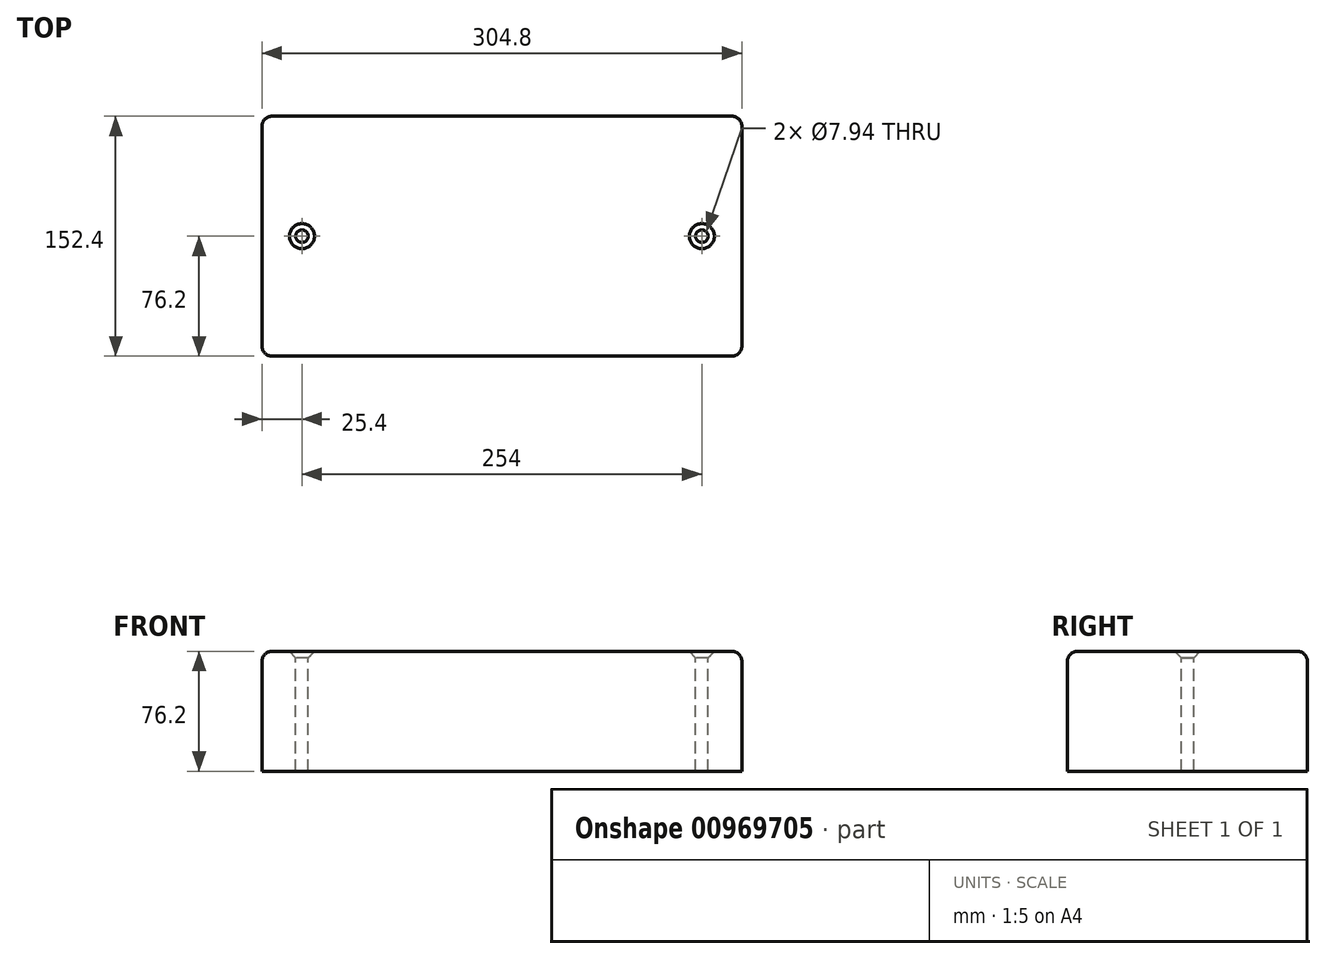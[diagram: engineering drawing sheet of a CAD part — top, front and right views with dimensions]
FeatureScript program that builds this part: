
annotation { "Feature Type Name" : "Feature", "Feature Type Description" : "" }
export const myFeature = defineFeature(function(context is Context, id is Id, definition is map)
    precondition{}
    {
        {
            var Q0;
            Q0=qCreatedBy(makeId("Top.planeOp"),FACE);
            var sketch = newSketch(context, id + "F0", { "sketchPlane" : qUnion([Q0])});
            skLineSegment(sketch, "E0.bottom", {"start": v(152.4, 76.2) * mm, "end": v(-152.4, 76.2) * mm});
            skLineSegment(sketch, "E0.top", {"start": v(152.4, -76.2) * mm, "end": v(-152.4, -76.2) * mm});
            skLineSegment(sketch, "E0.left", {"start": v(152.4, 76.2) * mm, "end": v(152.4, -76.2) * mm});
            skLineSegment(sketch, "E0.right", {"start": v(-152.4, 76.2) * mm, "end": v(-152.4, -76.2) * mm});
            skPoint(sketch, "E0.middle", {"position": v(0, 0) * mm});
            skSolve(sketch);
        }
        {
            var Q0;
            Q0 = qSketchRegion(id + "F0", true);
            extrude(context, id + "F1", {"entities" : qUnion([Q0]), "depth" : 76.2 * mm, "offsetDistance" : 25.4 * mm});
        }
        {
            var Q0;
            Q0=makeQuery(id+"F1.opExtrude","CAP_FACE",FACE,{"disambiguationData":[OSD([sQuery(id+"F0.wireOp",EDGE,"E0.bottom"),sQuery(id+"F0.wireOp",EDGE,"E0.top"),sQuery(id+"F0.wireOp",EDGE,"E0.left"),sQuery(id+"F0.wireOp",EDGE,"E0.right")])],"isStart":false});
            var sketch = newSketch(context, id + "F2", { "sketchPlane" : qUnion([Q0])});
            skPoint(sketch, "E1", {"position": v(-127, 0) * mm});
            skPoint(sketch, "E2", {"position": v(127, 0) * mm});
            skLineSegment(sketch, "E3", {"start": v(0, 0) * mm, "end": v(0, 76.2) * mm, "construction": true});
            skSolve(sketch);
        }
        {
            var Q0;
            Q0=sQuery(id+"F2.wireOp",VERTEX,"E1");
            var Q1;
            Q1=sQuery(id+"F2.wireOp",VERTEX,"E2");
            var Q2;
            Q2=makeQuery(id+"F1.opExtrude","SWEPT_BODY",BODY,{"disambiguationData":[OSD([sQuery(id+"F0.wireOp",EDGE,"E0.bottom"),sQuery(id+"F0.wireOp",EDGE,"E0.top"),sQuery(id+"F0.wireOp",EDGE,"E0.left"),sQuery(id+"F0.wireOp",EDGE,"E0.right")])]});
            hole(context, id + "F3", {"style" : HoleStyle.C_SINK, "endStyle" : HoleEndStyle.THROUGH, "holeDiameter" : 7.94 * mm, "cSinkDiameter" : 15.88 * mm, "cSinkAngle" : 85 * degree, "majorDiameter" : 6.35 * mm, "isTappedThrough" : true, "tappedDepth" : 12.7 * mm, "tapClearance" : 3, "locations" : qUnion([Q0, Q1]), "scope" : qUnion([Q2])});
        }
        {
            var Q0;
            Q0=makeQuery(id+"F1.opExtrude","CAP_EDGE",EDGE,{"disambiguationData":[OSD([sQuery(id+"F0.wireOp",EDGE,"E0.right")])],"isStart":false});
            var Q1;
            Q1=makeQuery(id+"F1.opExtrude","CAP_EDGE",EDGE,{"disambiguationData":[OSD([sQuery(id+"F0.wireOp",EDGE,"E0.left")])],"isStart":false});
            fillet(context, id + "F4", {"entities" : qUnion([Q0, Q1]), "radius" : 6.35 * mm, "tangentPropagation" : true, "allowEdgeOverflow" : false});
        }
        {
            var Q0;
            Q0=makeQuery(id+"F1.opExtrude","CAP_EDGE",EDGE,{"disambiguationData":[OSD([sQuery(id+"F0.wireOp",EDGE,"E0.top")])],"isStart":false});
            var Q1;
            Q1=makeQuery(id+"F1.opExtrude","CAP_EDGE",EDGE,{"disambiguationData":[OSD([sQuery(id+"F0.wireOp",EDGE,"E0.bottom")])],"isStart":false});
            fillet(context, id + "F5", {"entities" : qUnion([Q0, Q1]), "radius" : 6.35 * mm, "tangentPropagation" : true, "allowEdgeOverflow" : false});
        }
    });
